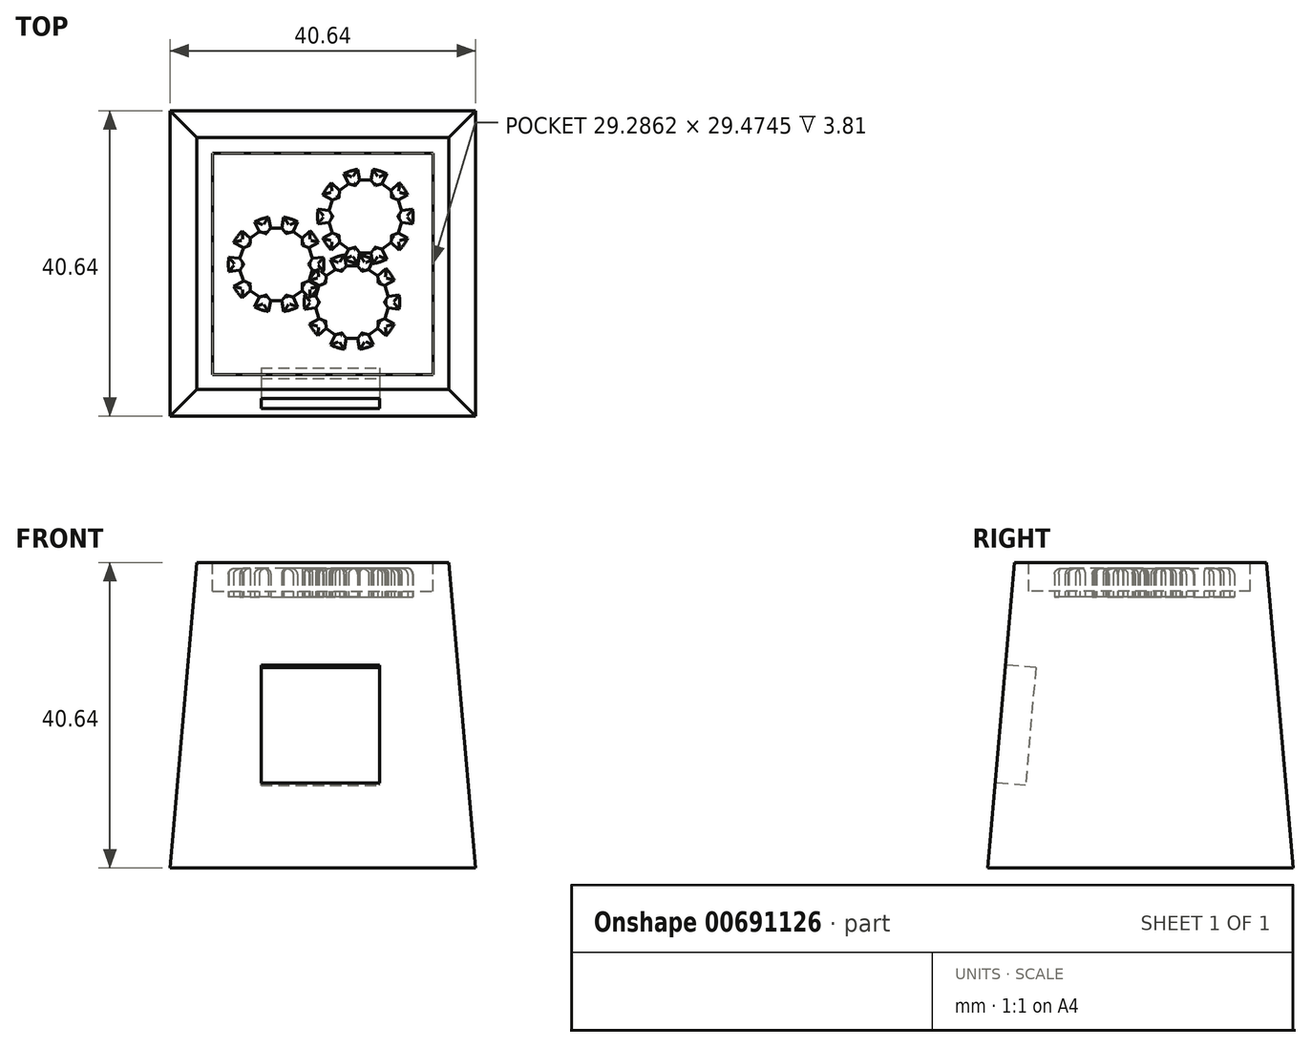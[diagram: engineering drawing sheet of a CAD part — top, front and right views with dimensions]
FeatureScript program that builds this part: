
annotation { "Feature Type Name" : "Feature", "Feature Type Description" : "" }
export const myFeature = defineFeature(function(context is Context, id is Id, definition is map)
    precondition{}
    {
        {
            var Q0;
            Q0=qCreatedBy(makeId("Top.planeOp"),FACE);
            var sketch = newSketch(context, id + "F0", { "sketchPlane" : qUnion([Q0])});
            skLineSegment(sketch, "E0.bottom", {"start": v(-40.64, 35.15) * mm, "end": v(0, 35.15) * mm});
            skLineSegment(sketch, "E0.top", {"start": v(-40.64, -5.49) * mm, "end": v(0, -5.49) * mm});
            skLineSegment(sketch, "E0.left", {"start": v(-40.64, 35.15) * mm, "end": v(-40.64, -5.49) * mm});
            skLineSegment(sketch, "E0.right", {"start": v(0, 35.15) * mm, "end": v(0, -5.49) * mm});
            skSolve(sketch);
        }
        {
            var Q0;
            Q0=makeQuery(id+"F0.imprint","IMPRINT",FACE,{"disambiguationData":[TD([[makeQuery(id+"F0.imprint","IMPRINT",EDGE,{"derivedFrom":sQuery(id+"F0.wireOp",EDGE,"E0.bottom")}),-1.0]])]});
            extrude(context, id + "F1", {"entities" : qUnion([Q0]), "depth" : 40.64 * mm, "offsetDistance" : 25.4 * mm, "hasDraft" : true, "draftAngle" : 5 * degree, "draftPullDirection" : true});
        }
        {
            var Q0;
            Q0=makeQuery(id+"F1.opExtrude","CAP_FACE",FACE,{"disambiguationData":[OSD([sQuery(id+"F0.wireOp",EDGE,"E0.bottom"),sQuery(id+"F0.wireOp",EDGE,"E0.top"),sQuery(id+"F0.wireOp",EDGE,"E0.left"),sQuery(id+"F0.wireOp",EDGE,"E0.right")])],"isStart":false});
            var sketch = newSketch(context, id + "F2", { "sketchPlane" : qUnion([Q0])});
            skLineSegment(sketch, "E1.bottom", {"start": v(-34.96, 29.47) * mm, "end": v(-5.68, 29.47) * mm});
            skLineSegment(sketch, "E1.top", {"start": v(-34.96, 0) * mm, "end": v(-5.68, 0) * mm});
            skLineSegment(sketch, "E1.left", {"start": v(-34.96, 29.47) * mm, "end": v(-34.96, 0) * mm});
            skLineSegment(sketch, "E1.right", {"start": v(-5.68, 29.47) * mm, "end": v(-5.68, 0) * mm});
            skSolve(sketch);
        }
        {
            var Q0;
            Q0=makeQuery(id+"F2.imprint","IMPRINT",FACE,{"disambiguationData":[TD([[makeQuery(id+"F2.imprint","IMPRINT",EDGE,{"derivedFrom":sQuery(id+"F2.wireOp",EDGE,"E1.bottom")}),-1.0]])]});
            extrude(context, id + "F3", {"entities" : qUnion([Q0]), "operationType" : NewBodyOperationType.REMOVE, "oppositeDirection" : true, "depth" : 3.8 * mm, "offsetDistance" : 25.4 * mm});
        }
        {
            var Q0;
            Q0=makeQuery(id+"F1.opExtrude","SWEPT_BODY",BODY,{"disambiguationData":[OSD([sQuery(id+"F0.wireOp",EDGE,"E0.bottom"),sQuery(id+"F0.wireOp",EDGE,"E0.top"),sQuery(id+"F0.wireOp",EDGE,"E0.left"),sQuery(id+"F0.wireOp",EDGE,"E0.right")])]});
            transform(context, id + "F4", {"entities" : qUnion([Q0]), "transformType" : TransformType.TRANSLATION_3D, "dx" : -21.34 * mm, "dy" : 23.1 * mm, "dz" : 0 * mm, "makeCopy" : false});
        }
        {
            var Q0;
            Q0=qCreatedBy(makeId("Top.planeOp"),FACE);
            var sketch = newSketch(context, id + "F5", { "sketchPlane" : qUnion([Q0])});
            skCircle(sketch, "E2", {"center": v(0, 0) * mm, "radius": 6.35 * mm});
            skSolve(sketch);
        }
        {
            var Q0;
            Q0=makeQuery(id+"F5.imprint","IMPRINT",FACE,{"disambiguationData":[TD([[makeQuery(id+"F5.imprint","IMPRINT",EDGE,{"derivedFrom":sQuery(id+"F5.wireOp",EDGE,"E2")}),1.0]])]});
            extrude(context, id + "F6", {"entities" : qUnion([Q0]), "depth" : 3.8 * mm, "offsetDistance" : 25.4 * mm});
        }
        {
            var Q0;
            Q0=qCreatedBy(makeId("Right.planeOp"),FACE);
            var sketch = newSketch(context, id + "F7", { "sketchPlane" : qUnion([Q0])});
            skLineSegment(sketch, "E3", {"start": v(0, 0) * mm, "end": v(0, 4.57) * mm});
            skSolve(sketch);
        }
        {
            var Q0;
            Q0=qCreatedBy(makeId("Top.planeOp"),FACE);
            var sketch = newSketch(context, id + "F8", { "sketchPlane" : qUnion([Q0])});
            skLineSegment(sketch, "E4", {"start": v(-0.74, 4.83) * mm, "end": v(0, 4.83) * mm});
            skLineSegment(sketch, "E5", {"start": v(-0.74, 4.83) * mm, "end": v(-1.24, 7.35) * mm});
            skLineSegment(sketch, "E6", {"start": v(-1.24, 7.35) * mm, "end": v(0, 7.35) * mm});
            skLineSegment(sketch, "E7.MirrorCS", {"start": v(1.24, 7.35) * mm, "end": v(0, 7.35) * mm});
            skLineSegment(sketch, "E8.MirrorCS", {"start": v(0.74, 4.83) * mm, "end": v(1.24, 7.35) * mm});
            skLineSegment(sketch, "E9.MirrorCS", {"start": v(0.74, 4.83) * mm, "end": v(0, 4.83) * mm});
            skSolve(sketch);
        }
        {
            var Q0;
            Q0=makeQuery(id+"F8.imprint","IMPRINT",FACE,{"disambiguationData":[TD([[makeQuery(id+"F8.imprint","IMPRINT",EDGE,{"derivedFrom":sQuery(id+"F8.wireOp",EDGE,"E4")}),1.0]])]});
            extrude(context, id + "F9", {"entities" : qUnion([Q0]), "depth" : 4.57 * mm, "offsetDistance" : 25.4 * mm});
        }
        {
            var Q0;
            Q0=makeQuery(id+"F9.opExtrude","SWEPT_BODY",BODY,{"disambiguationData":[OSD([sQuery(id+"F8.wireOp",EDGE,"E4"),sQuery(id+"F8.wireOp",EDGE,"E5"),sQuery(id+"F8.wireOp",EDGE,"E6"),sQuery(id+"F8.wireOp",EDGE,"E7.MirrorCS"),sQuery(id+"F8.wireOp",EDGE,"E8.MirrorCS"),sQuery(id+"F8.wireOp",EDGE,"E9.MirrorCS")])]});
            var Q1;
            Q1=sQuery(id+"F7.wireOp",EDGE,"E3");
            circularPattern(context, id + "F10", {"entities" : qUnion([Q0]), "axis" : qUnion([Q1]), "angle" : 360 * degree, "instanceCount" : 10, "equalSpace" : true});
        }
        {
            var Q0;
            Q0=makeQuery(id+"F9.opExtrude","SWEPT_BODY",BODY,{"disambiguationData":[OSD([sQuery(id+"F8.wireOp",EDGE,"E4"),sQuery(id+"F8.wireOp",EDGE,"E5"),sQuery(id+"F8.wireOp",EDGE,"E6"),sQuery(id+"F8.wireOp",EDGE,"E7.MirrorCS"),sQuery(id+"F8.wireOp",EDGE,"E8.MirrorCS"),sQuery(id+"F8.wireOp",EDGE,"E9.MirrorCS")])]});
            var Q1;
            Q1=makeQuery(id+"F10.opPattern","COPY",BODY,{"derivedFrom":makeQuery(id+"F9.opExtrude","SWEPT_BODY",BODY,{"disambiguationData":[OSD([sQuery(id+"F8.wireOp",EDGE,"E4"),sQuery(id+"F8.wireOp",EDGE,"E5"),sQuery(id+"F8.wireOp",EDGE,"E6"),sQuery(id+"F8.wireOp",EDGE,"E7.MirrorCS"),sQuery(id+"F8.wireOp",EDGE,"E8.MirrorCS"),sQuery(id+"F8.wireOp",EDGE,"E9.MirrorCS")])]}),"instanceName":"1"});
            var Q2;
            Q2=makeQuery(id+"F10.opPattern","COPY",BODY,{"derivedFrom":makeQuery(id+"F9.opExtrude","SWEPT_BODY",BODY,{"disambiguationData":[OSD([sQuery(id+"F8.wireOp",EDGE,"E4"),sQuery(id+"F8.wireOp",EDGE,"E5"),sQuery(id+"F8.wireOp",EDGE,"E6"),sQuery(id+"F8.wireOp",EDGE,"E7.MirrorCS"),sQuery(id+"F8.wireOp",EDGE,"E8.MirrorCS"),sQuery(id+"F8.wireOp",EDGE,"E9.MirrorCS")])]}),"instanceName":"2"});
            var Q3;
            Q3=makeQuery(id+"F10.opPattern","COPY",BODY,{"derivedFrom":makeQuery(id+"F9.opExtrude","SWEPT_BODY",BODY,{"disambiguationData":[OSD([sQuery(id+"F8.wireOp",EDGE,"E4"),sQuery(id+"F8.wireOp",EDGE,"E5"),sQuery(id+"F8.wireOp",EDGE,"E6"),sQuery(id+"F8.wireOp",EDGE,"E7.MirrorCS"),sQuery(id+"F8.wireOp",EDGE,"E8.MirrorCS"),sQuery(id+"F8.wireOp",EDGE,"E9.MirrorCS")])]}),"instanceName":"3"});
            var Q4;
            Q4=makeQuery(id+"F10.opPattern","COPY",BODY,{"derivedFrom":makeQuery(id+"F9.opExtrude","SWEPT_BODY",BODY,{"disambiguationData":[OSD([sQuery(id+"F8.wireOp",EDGE,"E4"),sQuery(id+"F8.wireOp",EDGE,"E5"),sQuery(id+"F8.wireOp",EDGE,"E6"),sQuery(id+"F8.wireOp",EDGE,"E7.MirrorCS"),sQuery(id+"F8.wireOp",EDGE,"E8.MirrorCS"),sQuery(id+"F8.wireOp",EDGE,"E9.MirrorCS")])]}),"instanceName":"4"});
            var Q5;
            Q5=makeQuery(id+"F10.opPattern","COPY",BODY,{"derivedFrom":makeQuery(id+"F9.opExtrude","SWEPT_BODY",BODY,{"disambiguationData":[OSD([sQuery(id+"F8.wireOp",EDGE,"E4"),sQuery(id+"F8.wireOp",EDGE,"E5"),sQuery(id+"F8.wireOp",EDGE,"E6"),sQuery(id+"F8.wireOp",EDGE,"E7.MirrorCS"),sQuery(id+"F8.wireOp",EDGE,"E8.MirrorCS"),sQuery(id+"F8.wireOp",EDGE,"E9.MirrorCS")])]}),"instanceName":"5"});
            var Q6;
            Q6=makeQuery(id+"F10.opPattern","COPY",BODY,{"derivedFrom":makeQuery(id+"F9.opExtrude","SWEPT_BODY",BODY,{"disambiguationData":[OSD([sQuery(id+"F8.wireOp",EDGE,"E4"),sQuery(id+"F8.wireOp",EDGE,"E5"),sQuery(id+"F8.wireOp",EDGE,"E6"),sQuery(id+"F8.wireOp",EDGE,"E7.MirrorCS"),sQuery(id+"F8.wireOp",EDGE,"E8.MirrorCS"),sQuery(id+"F8.wireOp",EDGE,"E9.MirrorCS")])]}),"instanceName":"6"});
            var Q7;
            Q7=makeQuery(id+"F10.opPattern","COPY",BODY,{"derivedFrom":makeQuery(id+"F9.opExtrude","SWEPT_BODY",BODY,{"disambiguationData":[OSD([sQuery(id+"F8.wireOp",EDGE,"E4"),sQuery(id+"F8.wireOp",EDGE,"E5"),sQuery(id+"F8.wireOp",EDGE,"E6"),sQuery(id+"F8.wireOp",EDGE,"E7.MirrorCS"),sQuery(id+"F8.wireOp",EDGE,"E8.MirrorCS"),sQuery(id+"F8.wireOp",EDGE,"E9.MirrorCS")])]}),"instanceName":"7"});
            var Q8;
            Q8=makeQuery(id+"F10.opPattern","COPY",BODY,{"derivedFrom":makeQuery(id+"F9.opExtrude","SWEPT_BODY",BODY,{"disambiguationData":[OSD([sQuery(id+"F8.wireOp",EDGE,"E4"),sQuery(id+"F8.wireOp",EDGE,"E5"),sQuery(id+"F8.wireOp",EDGE,"E6"),sQuery(id+"F8.wireOp",EDGE,"E7.MirrorCS"),sQuery(id+"F8.wireOp",EDGE,"E8.MirrorCS"),sQuery(id+"F8.wireOp",EDGE,"E9.MirrorCS")])]}),"instanceName":"8"});
            var Q9;
            Q9=makeQuery(id+"F10.opPattern","COPY",BODY,{"derivedFrom":makeQuery(id+"F9.opExtrude","SWEPT_BODY",BODY,{"disambiguationData":[OSD([sQuery(id+"F8.wireOp",EDGE,"E4"),sQuery(id+"F8.wireOp",EDGE,"E5"),sQuery(id+"F8.wireOp",EDGE,"E6"),sQuery(id+"F8.wireOp",EDGE,"E7.MirrorCS"),sQuery(id+"F8.wireOp",EDGE,"E8.MirrorCS"),sQuery(id+"F8.wireOp",EDGE,"E9.MirrorCS")])]}),"instanceName":"9"});
            var Q10;
            Q10=makeQuery(id+"F6.opExtrude","SWEPT_BODY",BODY,{"disambiguationData":[OSD([sQuery(id+"F5.wireOp",EDGE,"E2")])]});
            booleanBodies(context, id + "F11", {"operationType" : BooleanOperationType.SUBTRACTION, "tools" : qUnion([Q0, Q1, Q2, Q3, Q4, Q5, Q6, Q7, Q8, Q9]), "targets" : qUnion([Q10])});
        }
        {
            var Q0;
            Q0=makeQuery(id+"F6.opExtrude","SWEPT_BODY",BODY,{"disambiguationData":[OSD([sQuery(id+"F5.wireOp",EDGE,"E2")])]});
            transform(context, id + "F12", {"entities" : qUnion([Q0]), "transformType" : TransformType.TRANSLATION_3D, "dx" : -35.81 * mm, "dy" : 31.14 * mm, "dz" : 37.85 * mm, "makeCopy" : false});
        }
        {
            var Q0;
            Q0=makeQuery(id+"F6.opExtrude","CAP_FACE",FACE,{"disambiguationData":[OSD([sQuery(id+"F5.wireOp",EDGE,"E2")])],"isStart":false});
            fillet(context, id + "F13", {"entities" : qUnion([Q0]), "radius" : 0.76 * mm, "tangentPropagation" : true, "allowEdgeOverflow" : false});
        }
        {
            var Q0;
            Q0=makeQuery(id+"F6.opExtrude","SWEPT_BODY",BODY,{"disambiguationData":[OSD([sQuery(id+"F5.wireOp",EDGE,"E2")])]});
            transform(context, id + "F14", {"entities" : qUnion([Q0]), "transformType" : TransformType.TRANSLATION_3D, "dx" : -10.08 * mm, "dy" : 5.03 * mm, "dz" : 0 * mm, "makeCopy" : true});
        }
        {
            var Q0;
            Q0=makeQuery(id+"F14.opPattern","COPY",BODY,{"derivedFrom":makeQuery(id+"F6.opExtrude","SWEPT_BODY",BODY,{"disambiguationData":[OSD([sQuery(id+"F5.wireOp",EDGE,"E2")])]}),"instanceName":"1"});
            transform(context, id + "F15", {"entities" : qUnion([Q0]), "transformType" : TransformType.TRANSLATION_3D, "dx" : 11.86 * mm, "dy" : 6.38 * mm, "dz" : 0 * mm, "makeCopy" : true});
        }
        {
            var Q0;
            Q0=makeQuery(id+"F6.opExtrude","SWEPT_BODY",BODY,{"disambiguationData":[OSD([sQuery(id+"F5.wireOp",EDGE,"E2")])]});
            var Q1;
            Q1=makeQuery(id+"F14.opPattern","COPY",BODY,{"derivedFrom":makeQuery(id+"F6.opExtrude","SWEPT_BODY",BODY,{"disambiguationData":[OSD([sQuery(id+"F5.wireOp",EDGE,"E2")])]}),"instanceName":"1"});
            var Q2;
            Q2=makeQuery(id+"F15.opPattern","COPY",BODY,{"derivedFrom":makeQuery(id+"F14.opPattern","COPY",BODY,{"derivedFrom":makeQuery(id+"F6.opExtrude","SWEPT_BODY",BODY,{"disambiguationData":[OSD([sQuery(id+"F5.wireOp",EDGE,"E2")])]}),"instanceName":"1"}),"instanceName":"1"});
            transform(context, id + "F16", {"entities" : qUnion([Q0, Q1, Q2]), "transformType" : TransformType.TRANSLATION_3D, "dx" : -1.96 * mm, "dy" : 1.65 * mm, "dz" : 0 * mm, "makeCopy" : false});
        }
        {
            var Q0;
            Q0=makeQuery(id+"F1.opExtrude","SWEPT_FACE",FACE,{"disambiguationData":[OSD([sQuery(id+"F0.wireOp",EDGE,"E0.top")])]});
            var sketch = newSketch(context, id + "F17", { "sketchPlane" : qUnion([Q0])});
            skLineSegment(sketch, "E10.bottom", {"start": v(-49.87, 28.65) * mm, "end": v(-34.12, 28.65) * mm});
            skLineSegment(sketch, "E10.top", {"start": v(-49.87, 12.9) * mm, "end": v(-34.12, 12.9) * mm});
            skLineSegment(sketch, "E10.left", {"start": v(-49.87, 28.65) * mm, "end": v(-49.87, 12.9) * mm});
            skLineSegment(sketch, "E10.right", {"start": v(-34.12, 28.65) * mm, "end": v(-34.12, 12.9) * mm});
            skSolve(sketch);
        }
        {
            var Q0;
            Q0=makeQuery(id+"F17.imprint","IMPRINT",FACE,{"disambiguationData":[TD([[makeQuery(id+"F17.imprint","IMPRINT",EDGE,{"derivedFrom":sQuery(id+"F17.wireOp",EDGE,"E10.bottom")}),-1.0]])]});
            extrude(context, id + "F18", {"entities" : qUnion([Q0]), "operationType" : NewBodyOperationType.REMOVE, "oppositeDirection" : true, "depth" : 4.06 * mm, "offsetDistance" : 25.4 * mm});
        }
        {
            var Q0;
            Q0=makeQuery(id+"F1.opExtrude","SWEPT_BODY",BODY,{"disambiguationData":[OSD([sQuery(id+"F0.wireOp",EDGE,"E0.bottom"),sQuery(id+"F0.wireOp",EDGE,"E0.top"),sQuery(id+"F0.wireOp",EDGE,"E0.left"),sQuery(id+"F0.wireOp",EDGE,"E0.right")])]});
            transform(context, id + "F19", {"entities" : qUnion([Q0]), "transformType" : TransformType.TRANSLATION_3D, "dx" : 0 * mm, "dy" : 0 * mm, "dz" : 1.78 * mm, "makeCopy" : false});
        }
    });
